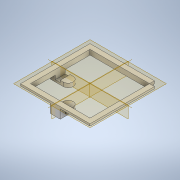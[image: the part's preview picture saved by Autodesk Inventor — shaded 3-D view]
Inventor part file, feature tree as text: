
AUTODESK INVENTOR PART (.ipt)
format: ipt  version: 2022.4 (Build 264492010, 492A)  size: 176,640 bytes
history: native  units: mm
features: extrude x5, sketch x3, chamfer x1, pattern_circular x1
ambient origin geometry x8: Origin, YZ Plane, XZ Plane, XY Plane, X Axis, Y Axis, Z Axis, Center Point
bodies: Solid1 (feature_tree)
feature tree (10):
  sketch  "Sketch1"  dims[d0=60.0mm d1=60.0mm]
  extrude  "Extrusion1"  Depth=60.0mm
  extrude  "Extrusion2"  Depth=2.0mm
  chamfer  "Chamfer1"  Distance=2.0mm
  extrude  "Extrusion3"  Depth=2.0mm TaperAngle=45.0deg
  sketch  "Sketch3"  dims[d6=5.0mm d7=0.0mm d8=3.0mm d9=2.0mm d10=45.0deg d11=10.0mm d12=11.0mm d13=0.0mm d14=10.0mm d15=5.0mm d16=10.0mm d17=3.0mm d18=5.0mm d19=2.0mm d20=0.0mm d21=4.0mm d22=0.0mm d23=20.0mm d24=-15.707963mm]
  extrude  "Extrusion4"  Depth=10.0mm
  extrude  "Extrusion5"  Depth=11.0mm TaperAngle=0.0deg
  pattern_circular  "Circular Pattern1"  [2 undecoded]
  sketch  "Sketch2"  dims[d2=5.0mm d3=2.0mm d4=2.0mm d5=0.0mm]
note: 2 required parameter values undecoded (feature->parameter linkage not recoverable at this tier; creation-order binding heuristic only, values carry confidence <= 0.55)
